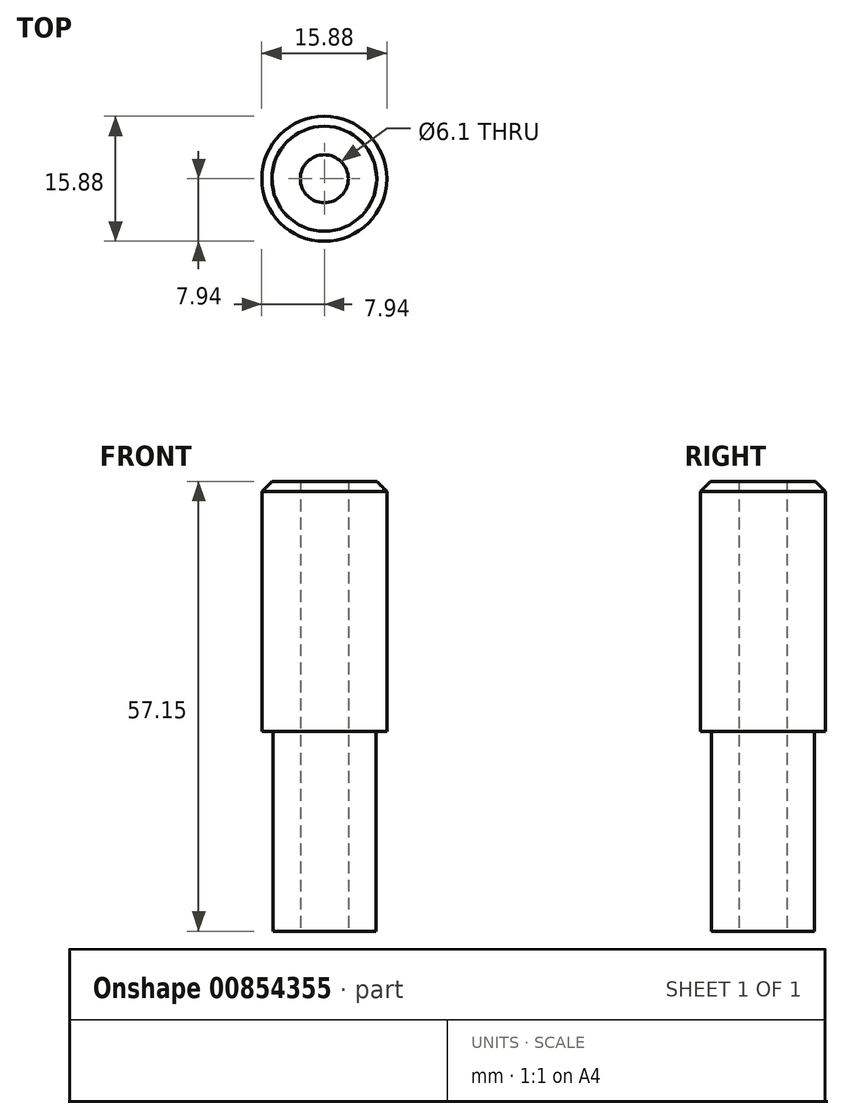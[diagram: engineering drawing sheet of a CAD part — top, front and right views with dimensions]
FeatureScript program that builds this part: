
annotation { "Feature Type Name" : "Feature", "Feature Type Description" : "" }
export const myFeature = defineFeature(function(context is Context, id is Id, definition is map)
    precondition{}
    {
        {
            var Q0;
            Q0=qCreatedBy(makeId("Top.planeOp"),FACE);
            var sketch = newSketch(context, id + "F0", { "sketchPlane" : qUnion([Q0])});
            skCircle(sketch, "E0", {"center": v(0, 0) * mm, "radius": 7.94 * mm, "construction": true});
            skCircle(sketch, "E1.0", {"center": v(0, 0) * mm, "radius": 6.54 * mm});
            skCircle(sketch, "E2", {"center": v(0, 0) * mm, "radius": 3.05 * mm});
            skSolve(sketch);
        }
        {
            var Q0;
            Q0=makeQuery(id+"F0.imprint","IMPRINT",FACE,{"disambiguationData":[TD([[makeQuery(id+"F0.imprint","IMPRINT",EDGE,{"derivedFrom":sQuery(id+"F0.wireOp",EDGE,"E1.0")}),1.0]])]});
            extrude(context, id + "F1", {"entities" : qUnion([Q0]), "depth" : 25.4 * mm, "offsetDistance" : 25.4 * mm});
        }
        {
            var Q0;
            Q0=qCreatedBy(makeId("Top.planeOp"),FACE);
            var sketch = newSketch(context, id + "F2", { "sketchPlane" : qUnion([Q0])});
            skCircle(sketch, "E3", {"center": v(0, 0) * mm, "radius": 7.94 * mm});
            skCircle(sketch, "E4", {"center": v(0, 0) * mm, "radius": 3.05 * mm});
            skSolve(sketch);
        }
        {
            var Q0;
            Q0=makeQuery(id+"F2.imprint","IMPRINT",FACE,{"disambiguationData":[TD([[makeQuery(id+"F2.imprint","IMPRINT",EDGE,{"derivedFrom":sQuery(id+"F2.wireOp",EDGE,"E3")}),1.0]])]});
            extrude(context, id + "F3", {"entities" : qUnion([Q0]), "operationType" : NewBodyOperationType.ADD, "depth" : 57.15 * mm, "offsetDistance" : 25.4 * mm, "hasSecondDirection" : true, "secondDirectionOppositeDirection" : true, "secondDirectionDepth" : -25.4 * mm});
        }
        {
            var Q0;
            Q0=makeQuery(id+"F3.opExtrude","CAP_EDGE",EDGE,{"disambiguationData":[OSD([sQuery(id+"F2.wireOp",EDGE,"E3")])],"isStart":false});
            chamfer(context, id + "F4", {"entities" : qUnion([Q0]), "width" : 1.27 * mm, "tangentPropagation" : true});
        }
    });
